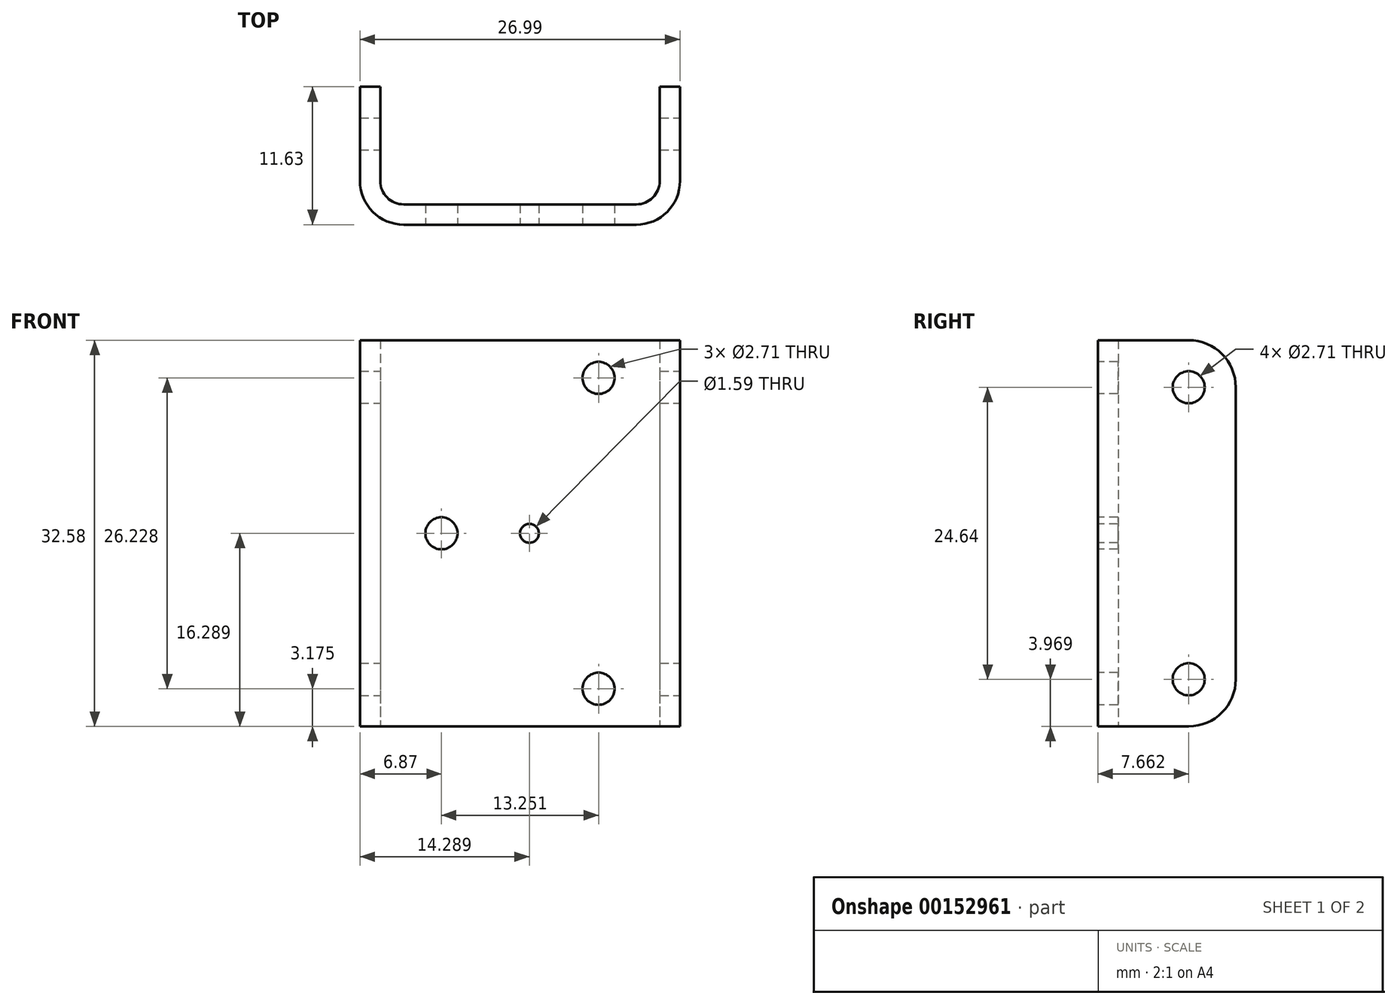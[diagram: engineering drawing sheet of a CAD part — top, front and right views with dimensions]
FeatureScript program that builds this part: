
annotation { "Feature Type Name" : "Feature", "Feature Type Description" : "" }
export const myFeature = defineFeature(function(context is Context, id is Id, definition is map)
    precondition{}
    {
        {
            var Q0;
            Q0=qCreatedBy(makeId("Top.planeOp"),FACE);
            var sketch = newSketch(context, id + "F0", { "sketchPlane" : qUnion([Q0])});
            skLineSegment(sketch, "E0.bottom", {"start": v(0, 0) * mm, "end": v(-23.57, 0) * mm});
            skLineSegment(sketch, "E0.top", {"start": v(1.7, -1.7) * mm, "end": v(-25.28, -1.7) * mm});
            skLineSegment(sketch, "E1.top", {"start": v(-23.57, 9.92) * mm, "end": v(-25.28, 9.92) * mm});
            skLineSegment(sketch, "E1.left", {"start": v(-23.57, 0) * mm, "end": v(-23.57, 9.92) * mm});
            skLineSegment(sketch, "E1.right", {"start": v(-25.28, -1.7) * mm, "end": v(-25.28, 9.92) * mm});
            skLineSegment(sketch, "E2.top", {"start": v(0, 9.92) * mm, "end": v(1.7, 9.92) * mm});
            skLineSegment(sketch, "E2.left", {"start": v(0, 0) * mm, "end": v(0, 9.92) * mm});
            skLineSegment(sketch, "E2.right", {"start": v(1.7, -1.7) * mm, "end": v(1.7, 9.92) * mm});
            skLineSegment(sketch, "E3", {"start": v(-11.78, 0) * mm, "end": v(-11.78, -1.7) * mm, "construction": true});
            skArc(sketch, "E4", {"start": v(-1.98, 0) * mm, "mid": v(-0.58, 0.58) * mm, "end": v(0, 1.98) * mm, "construction": true});
            skSolve(sketch);
        }
        {
            var Q0;
            Q0=qSketchRegion(id+"F0",true);
            extrude(context, id + "F1", {"entities" : qUnion([Q0]), "depth" : 32.58 * mm});
        }
        {
            var Q0;
            Q0=makeQuery(id+"F1.opExtrude","SWEPT_EDGE",EDGE,{"disambiguationData":[OSD([sQuery(id+"F0.wireOp",EDGE,"E0.top"),sQuery(id+"F0.wireOp",EDGE,"E2.right")])]});
            var Q1;
            Q1=makeQuery(id+"F1.opExtrude","SWEPT_EDGE",EDGE,{"disambiguationData":[OSD([sQuery(id+"F0.wireOp",EDGE,"E0.top"),sQuery(id+"F0.wireOp",EDGE,"E1.right")])]});
            var Q2;
            Q2=makeQuery(id+"FqNnmMD7oaRdpTN_1.opExtrude","CAP_EDGE",EDGE,{"disambiguationData":[OSD([sQuery(id+"FY5sMr6MULj5lJw_1.wireOp",EDGE,"W42EfhJi-fDm4-L9BW-folL-irsYfDskuzBk.top")])],"isStart":false});
            fillet(context, id + "F2", {"entities" : qUnion([Q0, Q1, Q2]), "radius" : 3.7 * mm, "tangentPropagation" : true, "allowEdgeOverflow" : false});
        }
        {
            var Q0;
            Q0=makeQuery(id+"F1.opExtrude","SWEPT_EDGE",EDGE,{"disambiguationData":[OSD([sQuery(id+"F0.wireOp",EDGE,"E0.bottom"),sQuery(id+"F0.wireOp",EDGE,"E2.left")])]});
            var Q1;
            Q1=makeQuery(id+"F1.opExtrude","SWEPT_EDGE",EDGE,{"disambiguationData":[OSD([sQuery(id+"F0.wireOp",EDGE,"E0.bottom"),sQuery(id+"F0.wireOp",EDGE,"E1.left")])]});
            fillet(context, id + "F3", {"entities" : qUnion([Q0, Q1]), "radius" : 1.98 * mm, "tangentPropagation" : true, "allowEdgeOverflow" : false});
        }
        {
            var Q0;
            Q0=makeQuery(id+"F1.opExtrude","SWEPT_FACE",FACE,{"disambiguationData":[OSD([sQuery(id+"F0.wireOp",EDGE,"E2.right")])]});
            var sketch = newSketch(context, id + "F4", { "sketchPlane" : qUnion([Q0])});
            skLineSegment(sketch, "E5.bottom", {"start": v(5.95, 0) * mm, "end": v(9.92, 0) * mm, "construction": true});
            skLineSegment(sketch, "E5.top", {"start": v(5.95, 3.97) * mm, "end": v(9.92, 3.97) * mm, "construction": true});
            skLineSegment(sketch, "E5.left", {"start": v(5.95, 0) * mm, "end": v(5.95, 3.97) * mm, "construction": true});
            skLineSegment(sketch, "E5.right", {"start": v(9.92, 0) * mm, "end": v(9.92, 3.97) * mm, "construction": true});
            skLineSegment(sketch, "E6.bottom", {"start": v(5.95, 32.58) * mm, "end": v(9.92, 32.58) * mm, "construction": true});
            skLineSegment(sketch, "E6.top", {"start": v(5.95, 28.6) * mm, "end": v(9.92, 28.6) * mm, "construction": true});
            skLineSegment(sketch, "E6.left", {"start": v(5.95, 32.58) * mm, "end": v(5.95, 28.6) * mm, "construction": true});
            skLineSegment(sketch, "E6.right", {"start": v(9.92, 32.58) * mm, "end": v(9.92, 28.6) * mm, "construction": true});
            skCircle(sketch, "E7", {"center": v(5.95, 3.97) * mm, "radius": 1.35 * mm});
            skCircle(sketch, "E8", {"center": v(5.95, 28.6) * mm, "radius": 1.35 * mm});
            skSolve(sketch);
        }
        {
            var Q0;
            Q0=qSketchRegion(id+"F4",true);
            var Q1;
            Q1=makeQuery(id+"F1.opExtrude","SWEPT_FACE",FACE,{"disambiguationData":[OSD([sQuery(id+"F0.wireOp",EDGE,"E1.right")])]});
            extrude(context, id + "F5", {"entities" : qUnion([Q0]), "operationType" : NewBodyOperationType.REMOVE, "endBound" : BoundingType.UP_TO_SURFACE, "oppositeDirection" : true, "endBoundEntityFace" : qUnion([Q1]), "depth" : 25.4 * mm});
        }
        {
            var Q0;
            Q0=makeQuery(id+"F1.opExtrude","CAP_EDGE",EDGE,{"disambiguationData":[OSD([sQuery(id+"F0.wireOp",EDGE,"E2.top")])],"isStart":false});
            var Q1;
            Q1=makeQuery(id+"F1.opExtrude","CAP_EDGE",EDGE,{"disambiguationData":[OSD([sQuery(id+"F0.wireOp",EDGE,"E1.top")])],"isStart":false});
            var Q2;
            Q2=makeQuery(id+"F1.opExtrude","CAP_EDGE",EDGE,{"disambiguationData":[OSD([sQuery(id+"F0.wireOp",EDGE,"E2.top")])],"isStart":true});
            var Q3;
            Q3=makeQuery(id+"F1.opExtrude","CAP_EDGE",EDGE,{"disambiguationData":[OSD([sQuery(id+"F0.wireOp",EDGE,"E1.top")])],"isStart":true});
            fillet(context, id + "F6", {"entities" : qUnion([Q0, Q1, Q2, Q3]), "radius" : 3.97 * mm, "tangentPropagation" : true, "allowEdgeOverflow" : false});
        }
        {
            var Q0;
            Q0=makeQuery(id+"F1.opExtrude","SWEPT_FACE",FACE,{"disambiguationData":[OSD([sQuery(id+"F0.wireOp",EDGE,"E0.top")])]});
            var sketch = newSketch(context, id + "F7", { "sketchPlane" : qUnion([Q0])});
            skLineSegment(sketch, "E9", {"start": v(-1.98, 16.29) * mm, "end": v(-11, 16.29) * mm, "construction": true});
            skCircle(sketch, "E10", {"center": v(-11, 16.29) * mm, "radius": 0.8 * mm});
            skLineSegment(sketch, "E11", {"start": v(-11, 16.29) * mm, "end": v(-5.16, 29.4) * mm, "construction": true});
            skLineSegment(sketch, "E12", {"start": v(-11, 16.29) * mm, "end": v(-18.4, 16.29) * mm, "construction": true});
            skLineSegment(sketch, "E13", {"start": v(-11, 16.29) * mm, "end": v(-5.16, 3.17) * mm, "construction": true});
            skLineSegment(sketch, "E14", {"start": v(-5.16, 3.17) * mm, "end": v(-5.16, 29.4) * mm, "construction": true});
            skLineSegment(sketch, "E15", {"start": v(-5.16, 29.4) * mm, "end": v(-18.4, 16.29) * mm, "construction": true});
            skLineSegment(sketch, "E16", {"start": v(-18.4, 16.29) * mm, "end": v(-5.16, 3.17) * mm, "construction": true});
            skLineSegment(sketch, "E17.bottom", {"start": v(-5.16, 29.4) * mm, "end": v(-1.98, 29.4) * mm, "construction": true});
            skLineSegment(sketch, "E17.top", {"start": v(-5.16, 32.58) * mm, "end": v(-1.98, 32.58) * mm, "construction": true});
            skLineSegment(sketch, "E17.left", {"start": v(-5.16, 29.4) * mm, "end": v(-5.16, 32.58) * mm, "construction": true});
            skLineSegment(sketch, "E17.right", {"start": v(-1.98, 29.4) * mm, "end": v(-1.98, 32.58) * mm, "construction": true});
            skLineSegment(sketch, "E18", {"start": v(-18.4, 16.29) * mm, "end": v(-21.58, 16.29) * mm, "construction": true});
            skCircle(sketch, "E19", {"center": v(-18.4, 16.29) * mm, "radius": 1.35 * mm});
            skCircle(sketch, "E20", {"center": v(-5.16, 29.4) * mm, "radius": 1.35 * mm});
            skCircle(sketch, "E21", {"center": v(-5.16, 3.17) * mm, "radius": 1.35 * mm});
            skSolve(sketch);
        }
        {
            var Q0;
            Q0 = qSketchRegion(id + "F7", true);
            var Q1;
            Q1=makeQuery(id+"F1.opExtrude","SWEPT_FACE",FACE,{"disambiguationData":[OSD([sQuery(id+"F0.wireOp",EDGE,"E0.bottom")])]});
            extrude(context, id + "F8", {"entities" : qUnion([Q0]), "operationType" : NewBodyOperationType.REMOVE, "endBound" : BoundingType.UP_TO_SURFACE, "oppositeDirection" : true, "endBoundEntityFace" : qUnion([Q1]), "depth" : 25.4 * mm});
        }
    });
